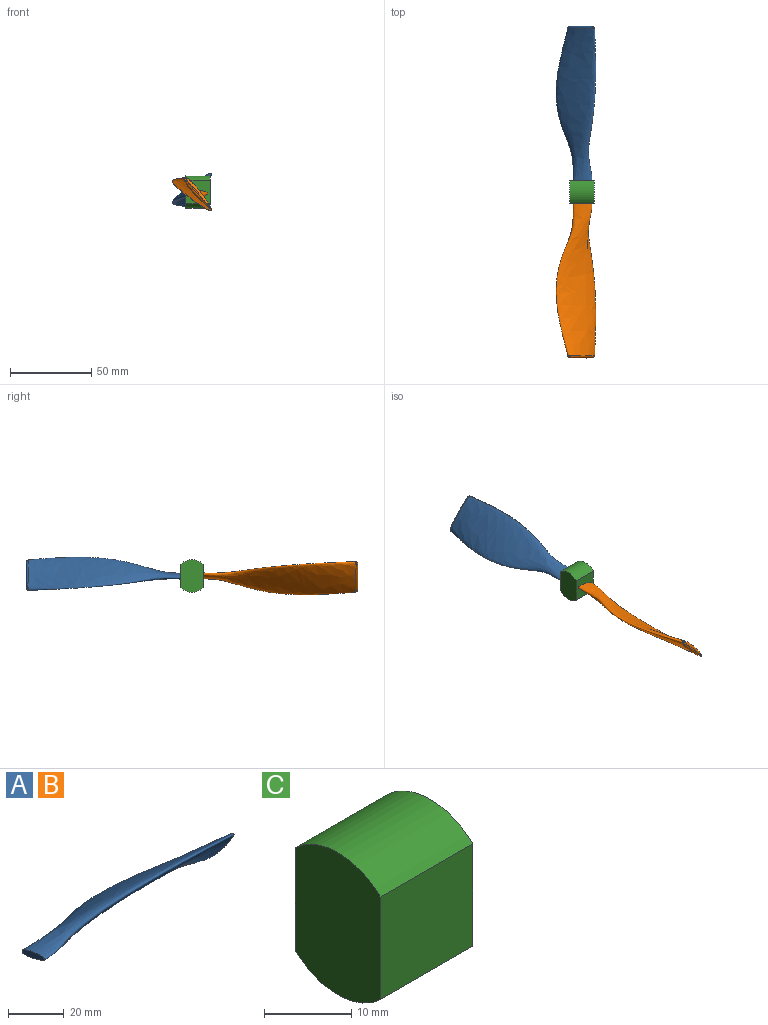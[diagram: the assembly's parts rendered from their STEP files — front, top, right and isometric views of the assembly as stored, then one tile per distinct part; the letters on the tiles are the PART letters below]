
ASSEMBLY  parts=3 mates=2
PART A: 9 faces, bbox 95x24.2x20.5 mm
  f0: plane 11.65x3.66mm, normal (-1,0,0), area 25.9mm2, adj f2
  f1: plane 10.82x9.46mm, normal (1,0,0), area 7.7mm2, adj f5,f6
  f2: bspline ~93.86x24.11mm, area 4462.3mm2, adj f0,f4,f5,f6,f7
  f3: bspline ~2.22x2.09mm, area 3.5mm2, adj f4,f5,f6
  f4: bspline ~1.64x1.59mm, area 1.7mm2, adj f2,f3,f6
  f5: bspline ~17.44x16.22mm, area 40.3mm2, adj f1,f2,f3,f8
  f6: bspline ~18.57x15.48mm, area 52.6mm2, adj f1,f2,f3,f4,f7,f8
  f7: bspline ~0.85x0.85mm, area 0.1mm2, adj f2,f6,f8
  f8: bspline ~5.48x4.74mm, area 2.7mm2, adj f5,f6,f7
PART B: same geometry as A
PART C: 6 faces, bbox 15x13.9x20 mm
  f0: cylinder r=10mm len=15mm, axis (-1,0,0), area 230.2mm2, adj f1,f3,f4,f5
  f1: plane 15x14.4mm, normal (0,-1,0), area 216mm2, adj f0,f2,f4,f5
  f2: cylinder r=10mm len=15mm, axis (-1,0,0), area 230.2mm2, adj f1,f3,f4,f5
  f3: plane 15x14.4mm, normal (0,1,0), area 216mm2, adj f0,f2,f4,f5
  f4: plane 20x13.88mm, normal (1,0,0), area 253.4mm2, adj f0,f1,f2,f3
  f5: plane 20x13.88mm, normal (-1,0,0), area 253.4mm2, adj f0,f1,f2,f3
PLACE A rot(axis=(0,0,1),90deg) t=(-54.97,63.01,-1.66)mm
PLACE B rot(axis=(0.71,-0.71,0),180deg) t=(-54.97,49.13,-0.97)mm
PLACE C t=(-63.43,79.66,-12.11)mm
MATE fastened A.f0 <-> C.f3  axis (0,-1,0) through (-55.93,63.01,-1.32)mm
MATE fastened B.f0 <-> C.f1  axis (0,1,0) through (-55.93,49.13,-1.32)mm
